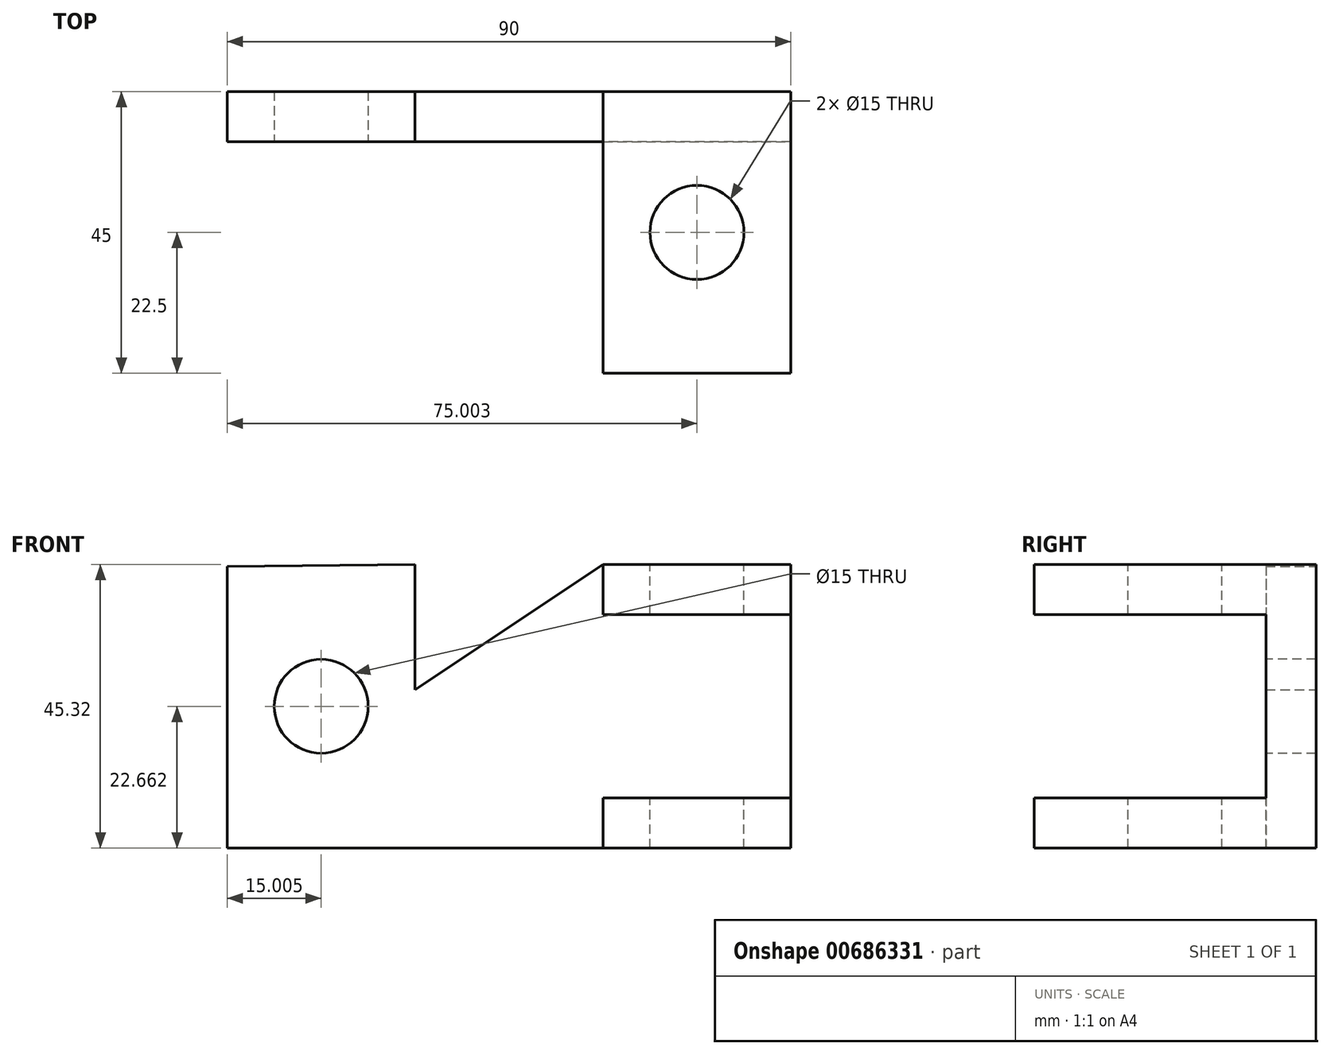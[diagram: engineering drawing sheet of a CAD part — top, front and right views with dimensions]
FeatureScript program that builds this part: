
annotation { "Feature Type Name" : "Feature", "Feature Type Description" : "" }
export const myFeature = defineFeature(function(context is Context, id is Id, definition is map)
    precondition{}
    {
        {
            var Q0;
            Q0=qCreatedBy(makeId("Front.planeOp"),FACE);
            var sketch = newSketch(context, id + "F0", { "sketchPlane" : qUnion([Q0])});
            skLineSegment(sketch, "E0", {"start": v(-56.68, 36) * mm, "end": v(-56.68, -9) * mm});
            skLineSegment(sketch, "E1", {"start": v(-56.68, -9) * mm, "end": v(33.32, -9) * mm});
            skLineSegment(sketch, "E2", {"start": v(33.32, -9) * mm, "end": v(33.32, 36.32) * mm});
            skLineSegment(sketch, "E3", {"start": v(33.32, 36.32) * mm, "end": v(3.32, 36.32) * mm});
            skLineSegment(sketch, "E4", {"start": v(3.32, 36.32) * mm, "end": v(-26.68, 16.32) * mm});
            skLineSegment(sketch, "E5", {"start": v(-26.68, 16.32) * mm, "end": v(-26.68, 36.32) * mm});
            skLineSegment(sketch, "E6", {"start": v(-26.68, 36.32) * mm, "end": v(-56.68, 36) * mm});
            skSolve(sketch);
        }
        {
            var Q0;
            Q0=makeQuery(id+"F0.imprint","IMPRINT",FACE,{"disambiguationData":[TD([[makeQuery(id+"F0.imprint","IMPRINT",EDGE,{"derivedFrom":sQuery(id+"F0.wireOp",EDGE,"E0")}),1.0]])]});
            extrude(context, id + "F1", {"entities" : qUnion([Q0]), "depth" : 8 * mm, "offsetDistance" : 25.4 * mm});
        }
        {
            var Q0;
            Q0=makeQuery(id+"F1.opExtrude","CAP_FACE",FACE,{"disambiguationData":[OSD([sQuery(id+"F0.wireOp",EDGE,"E0"),sQuery(id+"F0.wireOp",EDGE,"E1"),sQuery(id+"F0.wireOp",EDGE,"E2"),sQuery(id+"F0.wireOp",EDGE,"E3"),sQuery(id+"F0.wireOp",EDGE,"E4"),sQuery(id+"F0.wireOp",EDGE,"E5"),sQuery(id+"F0.wireOp",EDGE,"E6")])],"isStart":false});
            var sketch = newSketch(context, id + "F2", { "sketchPlane" : qUnion([Q0])});
            skLineSegment(sketch, "E7.bottom", {"start": v(3.32, 36.32) * mm, "end": v(33.32, 36.32) * mm});
            skLineSegment(sketch, "E7.top", {"start": v(3.32, 28.32) * mm, "end": v(33.32, 28.32) * mm});
            skLineSegment(sketch, "E7.left", {"start": v(3.32, 36.32) * mm, "end": v(3.32, 28.32) * mm});
            skLineSegment(sketch, "E7.right", {"start": v(33.32, 36.32) * mm, "end": v(33.32, 28.32) * mm});
            skLineSegment(sketch, "E8.bottom", {"start": v(33.32, -9) * mm, "end": v(3.32, -9) * mm});
            skLineSegment(sketch, "E8.top", {"start": v(33.32, -1) * mm, "end": v(3.32, -1) * mm});
            skLineSegment(sketch, "E8.left", {"start": v(33.32, -9) * mm, "end": v(33.32, -1) * mm});
            skLineSegment(sketch, "E8.right", {"start": v(3.32, -9) * mm, "end": v(3.32, -1) * mm});
            skSolve(sketch);
        }
        {
            var Q0;
            Q0=makeQuery(id+"F2.imprint","IMPRINT",FACE,{"disambiguationData":[TD([[makeQuery(id+"F2.imprint","IMPRINT",EDGE,{"derivedFrom":sQuery(id+"F2.wireOp",EDGE,"E8.bottom")}),1.0]])]});
            extrude(context, id + "F3", {"entities" : qUnion([Q0]), "operationType" : NewBodyOperationType.ADD, "depth" : 37 * mm, "offsetDistance" : 25.4 * mm});
        }
        {
            var Q0;
            Q0=makeQuery(id+"F1.opExtrude","CAP_FACE",FACE,{"disambiguationData":[OSD([sQuery(id+"F0.wireOp",EDGE,"E0"),sQuery(id+"F0.wireOp",EDGE,"E1"),sQuery(id+"F0.wireOp",EDGE,"E2"),sQuery(id+"F0.wireOp",EDGE,"E3"),sQuery(id+"F0.wireOp",EDGE,"E4"),sQuery(id+"F0.wireOp",EDGE,"E5"),sQuery(id+"F0.wireOp",EDGE,"E6")])],"isStart":false});
            var sketch = newSketch(context, id + "F4", { "sketchPlane" : qUnion([Q0])});
            skLineSegment(sketch, "E9.bottom", {"start": v(3.32, 36.32) * mm, "end": v(33.32, 36.32) * mm});
            skLineSegment(sketch, "E9.top", {"start": v(3.32, 28.32) * mm, "end": v(33.32, 28.32) * mm});
            skLineSegment(sketch, "E9.left", {"start": v(3.32, 36.32) * mm, "end": v(3.32, 28.32) * mm});
            skLineSegment(sketch, "E9.right", {"start": v(33.32, 36.32) * mm, "end": v(33.32, 28.32) * mm});
            skSolve(sketch);
        }
        {
            var Q0;
            Q0=makeQuery(id+"F4.imprint","IMPRINT",FACE,{"disambiguationData":[TD([[makeQuery(id+"F4.imprint","IMPRINT",EDGE,{"derivedFrom":sQuery(id+"F4.wireOp",EDGE,"E9.bottom")}),1.0]])]});
            extrude(context, id + "F5", {"entities" : qUnion([Q0]), "operationType" : NewBodyOperationType.ADD, "depth" : 37 * mm, "offsetDistance" : 25.4 * mm});
        }
        {
            var Q0;
            Q0=makeQuery(id+"F5.boolean.opBoolean","MERGE",FACE,{"derivedFrom":[makeQuery(id+"F1.opExtrude","SWEPT_FACE",FACE,{"disambiguationData":[OSD([sQuery(id+"F0.wireOp",EDGE,"E3")])]}),makeQuery(id+"F5.opExtrude","SWEPT_FACE",FACE,{"disambiguationData":[OSD([sQuery(id+"F4.wireOp",EDGE,"E9.bottom")])]})]});
            var sketch = newSketch(context, id + "F6", { "sketchPlane" : qUnion([Q0])});
            skCircle(sketch, "E10", {"center": v(18.32, -22.5) * mm, "radius": 7.5 * mm});
            skSolve(sketch);
        }
        {
            var Q0;
            Q0 = qSketchRegion(id + "F6", true);
            extrude(context, id + "F7", {"entities" : qUnion([Q0]), "operationType" : NewBodyOperationType.REMOVE, "oppositeDirection" : true, "depth" : 81.03 * mm, "offsetDistance" : 25.4 * mm});
        }
        {
            var Q0;
            Q0=makeQuery(id+"F1.opExtrude","CAP_FACE",FACE,{"disambiguationData":[OSD([sQuery(id+"F0.wireOp",EDGE,"E0"),sQuery(id+"F0.wireOp",EDGE,"E1"),sQuery(id+"F0.wireOp",EDGE,"E2"),sQuery(id+"F0.wireOp",EDGE,"E3"),sQuery(id+"F0.wireOp",EDGE,"E4"),sQuery(id+"F0.wireOp",EDGE,"E5"),sQuery(id+"F0.wireOp",EDGE,"E6")])],"isStart":false});
            var sketch = newSketch(context, id + "F8", { "sketchPlane" : qUnion([Q0])});
            skCircle(sketch, "E11", {"center": v(-41.68, 13.66) * mm, "radius": 7.5 * mm});
            skSolve(sketch);
        }
        {
            var Q0;
            Q0 = qSketchRegion(id + "F8", true);
            extrude(context, id + "F9", {"entities" : qUnion([Q0]), "operationType" : NewBodyOperationType.REMOVE, "oppositeDirection" : true, "depth" : 57.15 * mm, "offsetDistance" : 25.4 * mm});
        }
    });
